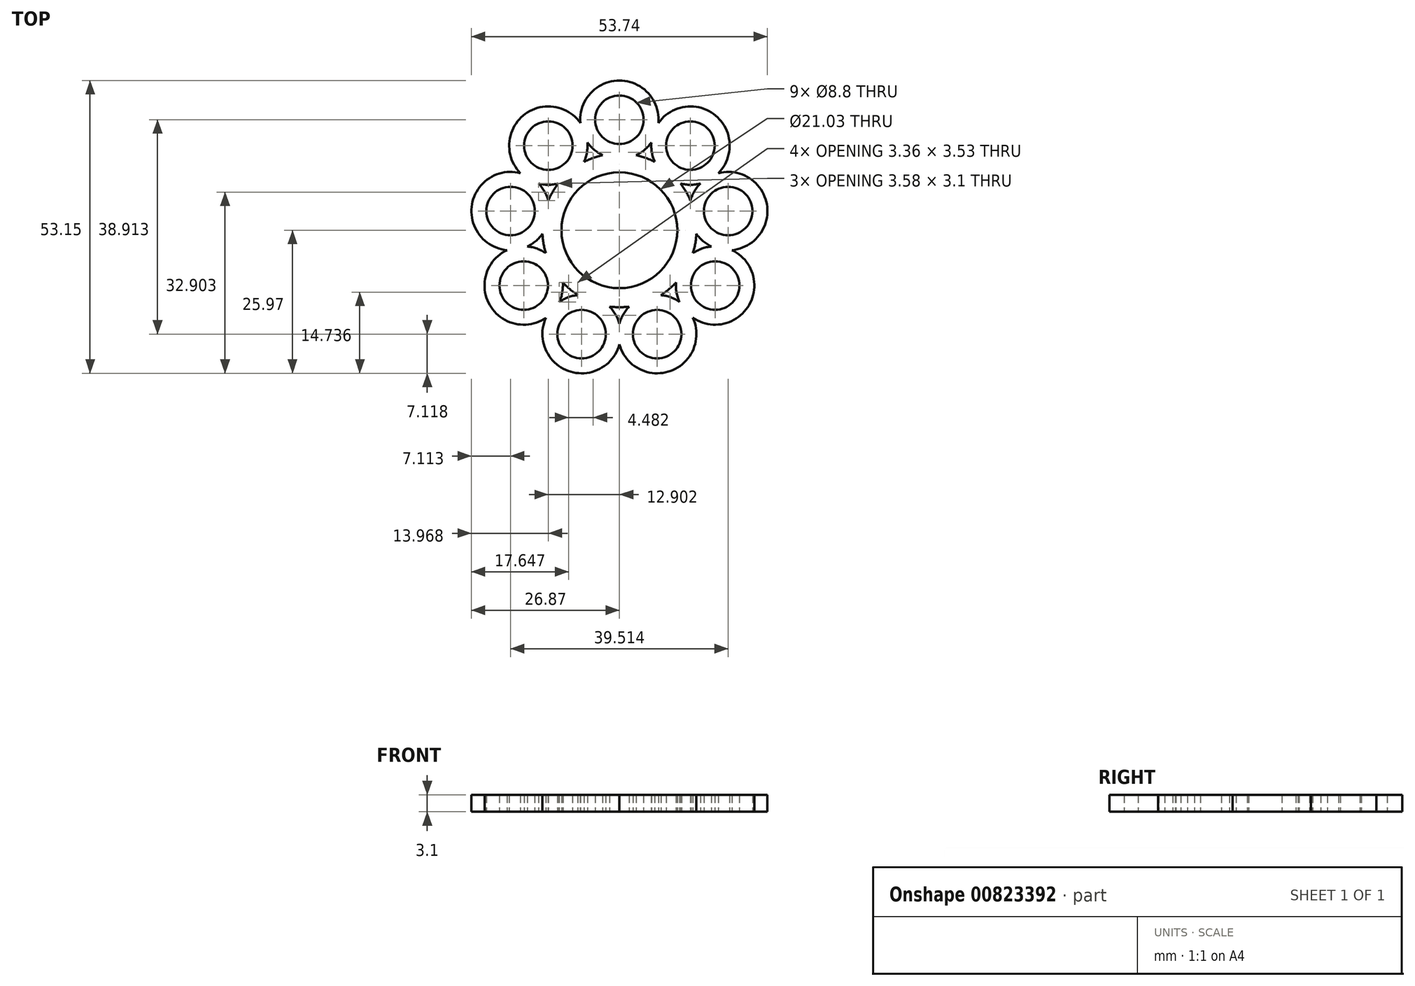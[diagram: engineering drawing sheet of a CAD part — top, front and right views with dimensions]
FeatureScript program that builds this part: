
annotation { "Feature Type Name" : "Feature", "Feature Type Description" : "" }
export const myFeature = defineFeature(function(context is Context, id is Id, definition is map)
    precondition{}
    {
        {
            var Q0;
            Q0=qCreatedBy(makeId("Top.planeOp"),FACE);
            var sketch = newSketch(context, id + "F0", { "sketchPlane" : qUnion([Q0])});
            skArc(sketch, "E0", {"start": v(3.6, 9.88) * mm, "mid": v(0, 10.51) * mm, "end": v(-3.6, 9.88) * mm});
            skArc(sketch, "E1", {"start": v(-3.06, 13.64) * mm, "mid": v(-3.93, 13.41) * mm, "end": v(-4.78, 13.13) * mm});
            skCircle(sketch, "E2", {"center": v(0, 20.06) * mm, "radius": 4.4 * mm});
            skArc(sketch, "E3", {"start": v(3.06, 13.64) * mm, "mid": v(4.58, 14.62) * mm, "end": v(5.8, 15.94) * mm});
            skArc(sketch, "E4.trimOffspring", {"start": v(4.78, 13.13) * mm, "mid": v(3.93, 13.41) * mm, "end": v(3.06, 13.64) * mm});
            skArc(sketch, "E5.1.0", {"start": v(-4.78, 13.13) * mm, "mid": v(-5.61, 12.8) * mm, "end": v(-6.42, 12.42) * mm});
            skArc(sketch, "E5.1.1", {"start": v(-3.6, 9.88) * mm, "mid": v(-6.76, 8.05) * mm, "end": v(-9.1, 5.26) * mm});
            skArc(sketch, "E5.1.2", {"start": v(-6.42, 12.42) * mm, "mid": v(-5.89, 14.14) * mm, "end": v(-5.8, 15.94) * mm});
            skArc(sketch, "E5.1.3", {"start": v(-11.11, 8.48) * mm, "mid": v(-11.63, 7.75) * mm, "end": v(-12.1, 6.99) * mm});
            skCircle(sketch, "E5.1.4", {"center": v(-12.9, 15.37) * mm, "radius": 4.4 * mm});
            skArc(sketch, "E5.2.0", {"start": v(-12.1, 6.99) * mm, "mid": v(-12.53, 6.2) * mm, "end": v(-12.9, 5.38) * mm});
            skArc(sketch, "E5.2.1", {"start": v(-9.1, 5.26) * mm, "mid": v(-10.35, 1.83) * mm, "end": v(-10.35, -1.83) * mm});
            skArc(sketch, "E5.2.2", {"start": v(-12.9, 5.38) * mm, "mid": v(-13.6, 7.05) * mm, "end": v(-14.7, 8.48) * mm});
            skArc(sketch, "E5.2.3", {"start": v(-13.96, -0.65) * mm, "mid": v(-13.9, -1.54) * mm, "end": v(-13.77, -2.43) * mm});
            skCircle(sketch, "E5.2.4", {"center": v(-19.76, 3.48) * mm, "radius": 4.4 * mm});
            skArc(sketch, "E5.3.0", {"start": v(-13.77, -2.43) * mm, "mid": v(-13.58, -3.3) * mm, "end": v(-13.34, -4.17) * mm});
            skArc(sketch, "E5.3.1", {"start": v(-10.35, -1.83) * mm, "mid": v(-9.1, -5.26) * mm, "end": v(-6.76, -8.05) * mm});
            skArc(sketch, "E5.3.2", {"start": v(-13.34, -4.17) * mm, "mid": v(-14.95, -3.34) * mm, "end": v(-16.7, -2.95) * mm});
            skArc(sketch, "E5.3.3", {"start": v(-10.28, -9.47) * mm, "mid": v(-9.65, -10.1) * mm, "end": v(-8.98, -10.7) * mm});
            skCircle(sketch, "E5.3.4", {"center": v(-17.37, -10.03) * mm, "radius": 4.4 * mm});
            skArc(sketch, "E5.4.0", {"start": v(-8.98, -10.7) * mm, "mid": v(-8.28, -11.26) * mm, "end": v(-7.54, -11.77) * mm});
            skArc(sketch, "E5.4.1", {"start": v(-6.76, -8.05) * mm, "mid": v(-3.6, -9.88) * mm, "end": v(0, -10.51) * mm});
            skArc(sketch, "E5.4.2", {"start": v(-7.54, -11.77) * mm, "mid": v(-9.3, -12.17) * mm, "end": v(-10.9, -13) * mm});
            skArc(sketch, "E5.4.3", {"start": v(-1.79, -13.86) * mm, "mid": v(-0.9, -13.95) * mm, "end": v(0, -13.98) * mm});
            skCircle(sketch, "E5.4.4", {"center": v(-6.86, -18.85) * mm, "radius": 4.4 * mm});
            skArc(sketch, "E5.5.0", {"start": v(0, -13.98) * mm, "mid": v(0.9, -13.95) * mm, "end": v(1.79, -13.86) * mm});
            skArc(sketch, "E5.5.1", {"start": v(0, -10.51) * mm, "mid": v(3.6, -9.88) * mm, "end": v(6.76, -8.05) * mm});
            skArc(sketch, "E5.5.2", {"start": v(1.79, -13.86) * mm, "mid": v(0.7, -15.3) * mm, "end": v(0, -16.97) * mm});
            skArc(sketch, "E5.5.3", {"start": v(7.54, -11.77) * mm, "mid": v(8.28, -11.26) * mm, "end": v(8.98, -10.7) * mm});
            skCircle(sketch, "E5.5.4", {"center": v(6.86, -18.85) * mm, "radius": 4.4 * mm});
            skArc(sketch, "E5.6.0", {"start": v(8.98, -10.7) * mm, "mid": v(9.65, -10.1) * mm, "end": v(10.28, -9.47) * mm});
            skArc(sketch, "E5.6.1", {"start": v(6.76, -8.05) * mm, "mid": v(9.1, -5.26) * mm, "end": v(10.35, -1.83) * mm});
            skArc(sketch, "E5.6.2", {"start": v(10.28, -9.47) * mm, "mid": v(10.37, -11.27) * mm, "end": v(10.9, -13) * mm});
            skArc(sketch, "E5.6.3", {"start": v(13.34, -4.17) * mm, "mid": v(13.58, -3.3) * mm, "end": v(13.77, -2.43) * mm});
            skCircle(sketch, "E5.6.4", {"center": v(17.37, -10.03) * mm, "radius": 4.4 * mm});
            skArc(sketch, "E5.7.0", {"start": v(13.77, -2.43) * mm, "mid": v(13.9, -1.54) * mm, "end": v(13.96, -0.65) * mm});
            skArc(sketch, "E5.7.1", {"start": v(10.35, -1.83) * mm, "mid": v(10.35, 1.83) * mm, "end": v(9.1, 5.26) * mm});
            skArc(sketch, "E5.7.2", {"start": v(13.96, -0.65) * mm, "mid": v(15.19, -1.97) * mm, "end": v(16.7, -2.95) * mm});
            skArc(sketch, "E5.7.3", {"start": v(12.9, 5.38) * mm, "mid": v(12.53, 6.2) * mm, "end": v(12.1, 6.99) * mm});
            skCircle(sketch, "E5.7.4", {"center": v(19.76, 3.48) * mm, "radius": 4.4 * mm});
            skArc(sketch, "E6.3.8.0", {"start": v(12.1, 6.99) * mm, "mid": v(11.63, 7.75) * mm, "end": v(11.11, 8.48) * mm});
            skArc(sketch, "E6.4.8.0", {"start": v(9.1, 5.26) * mm, "mid": v(6.76, 8.05) * mm, "end": v(3.6, 9.88) * mm});
            skArc(sketch, "E6.8.8.0", {"start": v(11.11, 8.48) * mm, "mid": v(12.9, 8.25) * mm, "end": v(14.7, 8.48) * mm});
            skArc(sketch, "E6.12.8.0", {"start": v(6.42, 12.42) * mm, "mid": v(5.61, 12.8) * mm, "end": v(4.78, 13.13) * mm});
            skCircle(sketch, "E6.16.8.0", {"center": v(12.9, 15.37) * mm, "radius": 4.4 * mm});
            skArc(sketch, "E7.trimOffspring", {"start": v(-5.8, 15.94) * mm, "mid": v(-4.58, 14.62) * mm, "end": v(-3.06, 13.64) * mm});
            skArc(sketch, "E8.trimOffspring", {"start": v(-14.7, 8.48) * mm, "mid": v(-12.9, 8.25) * mm, "end": v(-11.11, 8.48) * mm});
            skArc(sketch, "E9.trimOffspring", {"start": v(-16.7, -2.95) * mm, "mid": v(-15.19, -1.97) * mm, "end": v(-13.96, -0.65) * mm});
            skArc(sketch, "E10.trimOffspring", {"start": v(-10.9, -13) * mm, "mid": v(-10.37, -11.27) * mm, "end": v(-10.28, -9.47) * mm});
            skArc(sketch, "E11.trimOffspring", {"start": v(0, -16.97) * mm, "mid": v(-0.7, -15.3) * mm, "end": v(-1.79, -13.86) * mm});
            skArc(sketch, "E12.trimOffspring", {"start": v(10.9, -13) * mm, "mid": v(9.3, -12.17) * mm, "end": v(7.54, -11.77) * mm});
            skArc(sketch, "E13.trimOffspring", {"start": v(16.7, -2.95) * mm, "mid": v(14.95, -3.34) * mm, "end": v(13.34, -4.17) * mm});
            skArc(sketch, "E14.trimOffspring", {"start": v(14.7, 8.48) * mm, "mid": v(13.6, 7.05) * mm, "end": v(12.9, 5.38) * mm});
            skArc(sketch, "E15.trimOffspring", {"start": v(5.8, 15.94) * mm, "mid": v(5.89, 14.14) * mm, "end": v(6.42, 12.42) * mm});
            skArc(sketch, "E16.trimOffspring", {"start": v(17.96, 10.37) * mm, "mid": v(17.47, 20.82) * mm, "end": v(7.1, 19.49) * mm});
            skArc(sketch, "E17.trimOffspring", {"start": v(20.42, -3.6) * mm, "mid": v(26.76, 4.72) * mm, "end": v(17.96, 10.37) * mm});
            skArc(sketch, "E18.trimOffspring", {"start": v(13.33, -15.89) * mm, "mid": v(23.54, -13.59) * mm, "end": v(20.42, -3.6) * mm});
            skArc(sketch, "E19.trimOffspring", {"start": v(0, -20.74) * mm, "mid": v(9.3, -25.54) * mm, "end": v(13.33, -15.89) * mm});
            skArc(sketch, "E20.trimOffspring", {"start": v(-13.33, -15.89) * mm, "mid": v(-9.3, -25.54) * mm, "end": v(0, -20.74) * mm});
            skArc(sketch, "E21.trimOffspring", {"start": v(-20.42, -3.6) * mm, "mid": v(-23.54, -13.59) * mm, "end": v(-13.33, -15.89) * mm});
            skArc(sketch, "E22.trimOffspring", {"start": v(-17.96, 10.37) * mm, "mid": v(-26.76, 4.72) * mm, "end": v(-20.42, -3.6) * mm});
            skArc(sketch, "E23.trimOffspring", {"start": v(-7.1, 19.49) * mm, "mid": v(-17.47, 20.82) * mm, "end": v(-17.96, 10.37) * mm});
            skArc(sketch, "E24.trimOffspring", {"start": v(7.1, 19.49) * mm, "mid": v(0, 27.18) * mm, "end": v(-7.1, 19.49) * mm});
            skSolve(sketch);
        }
        {
            var Q0;
            Q0 = qSketchRegion(id + "F0", true);
            extrude(context, id + "F1", {"entities" : qUnion([Q0]), "depth" : 3.1 * mm, "offsetDistance" : 25 * mm});
        }
    });
